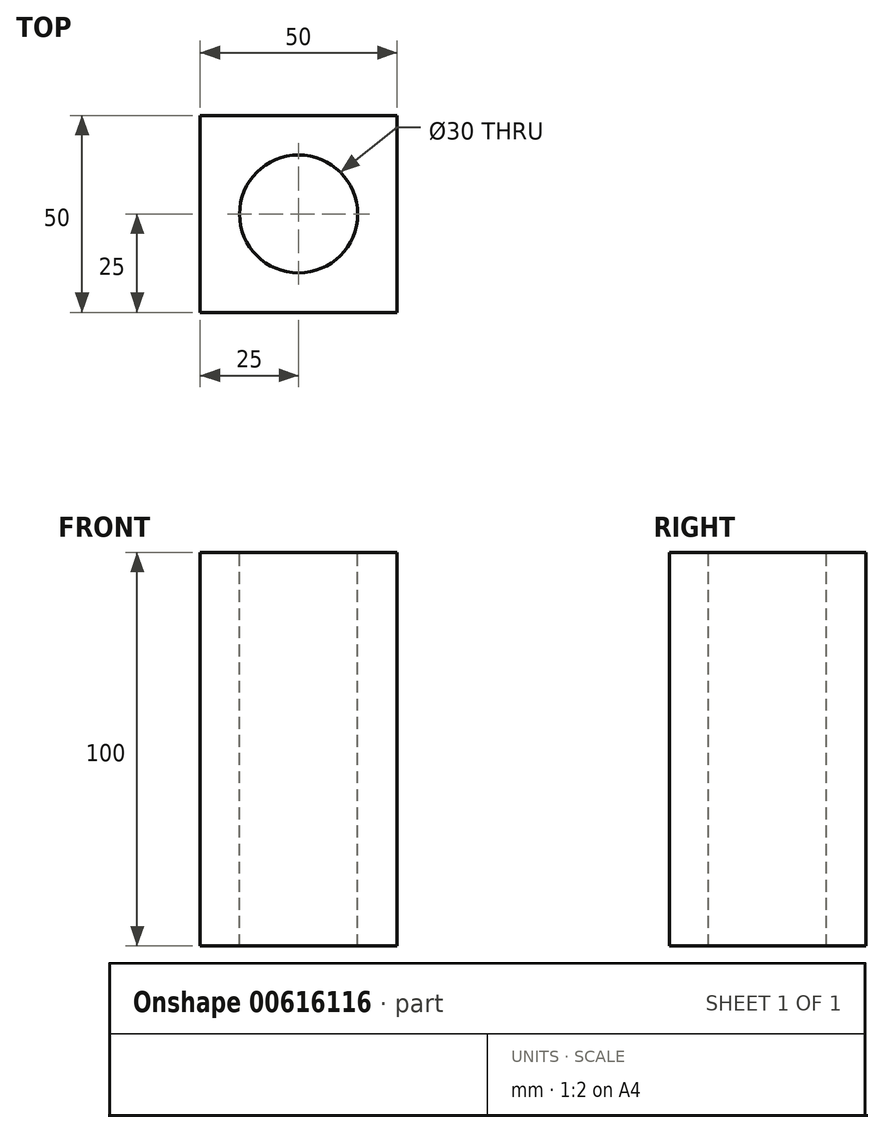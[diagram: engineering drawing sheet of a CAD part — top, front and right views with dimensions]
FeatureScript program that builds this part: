
annotation { "Feature Type Name" : "Feature", "Feature Type Description" : "" }
export const myFeature = defineFeature(function(context is Context, id is Id, definition is map)
    precondition{}
    {
        {
            var Q0;
            Q0=qCreatedBy(makeId("Top.planeOp"),FACE);
            var sketch = newSketch(context, id + "F0", { "sketchPlane" : qUnion([Q0])});
            skLineSegment(sketch, "E0.bottom", {"start": v(-25, 25) * mm, "end": v(25, 25) * mm});
            skLineSegment(sketch, "E0.top", {"start": v(-25, -25) * mm, "end": v(25, -25) * mm});
            skLineSegment(sketch, "E0.left", {"start": v(-25, 25) * mm, "end": v(-25, -25) * mm});
            skLineSegment(sketch, "E0.right", {"start": v(25, 25) * mm, "end": v(25, -25) * mm});
            skPoint(sketch, "E0.middle", {"position": v(0, 0) * mm});
            skSolve(sketch);
        }
        {
            var Q0;
            Q0=makeQuery(id+"F0.imprint","IMPRINT",FACE,{"disambiguationData":[TD([[makeQuery(id+"F0.imprint","IMPRINT",EDGE,{"derivedFrom":sQuery(id+"F0.wireOp",EDGE,"E0.bottom")}),-1.0]])]});
            extrude(context, id + "F1", {"entities" : qUnion([Q0]), "depth" : 50 * mm, "offsetDistance" : 25 * mm});
        }
        {
            var Q0;
            Q0=makeQuery(id+"F1.opExtrude","CAP_FACE",FACE,{"disambiguationData":[OSD([sQuery(id+"F0.wireOp",EDGE,"E0.bottom"),sQuery(id+"F0.wireOp",EDGE,"E0.top"),sQuery(id+"F0.wireOp",EDGE,"E0.left"),sQuery(id+"F0.wireOp",EDGE,"E0.right")])],"isStart":false});
            var sketch = newSketch(context, id + "F2", { "sketchPlane" : qUnion([Q0])});
            skCircle(sketch, "E1", {"center": v(0, 0) * mm, "radius": 15 * mm});
            skSolve(sketch);
        }
        {
            var Q0;
            Q0 = qSketchRegion(id + "F2", true);
            extrude(context, id + "F3", {"entities" : qUnion([Q0]), "operationType" : NewBodyOperationType.REMOVE, "oppositeDirection" : true, "depth" : 50 * mm, "offsetDistance" : 25 * mm});
        }
        {
            var Q0;
            Q0=makeQuery(id+"F1.opExtrude","CAP_FACE",FACE,{"disambiguationData":[OSD([sQuery(id+"F0.wireOp",EDGE,"E0.bottom"),sQuery(id+"F0.wireOp",EDGE,"E0.top"),sQuery(id+"F0.wireOp",EDGE,"E0.left"),sQuery(id+"F0.wireOp",EDGE,"E0.right")])],"isStart":false});
            extrude(context, id + "F4", {"entities" : qUnion([Q0]), "operationType" : NewBodyOperationType.ADD, "depth" : 50 * mm, "offsetDistance" : 25 * mm});
        }
    });
